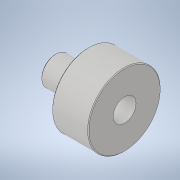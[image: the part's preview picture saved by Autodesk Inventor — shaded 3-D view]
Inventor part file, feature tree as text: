
AUTODESK INVENTOR PART (.ipt)
format: ipt  version: 2021 (Build 250183000, 183)  size: 119,808 bytes
history: native  units: in
note: dims shown in document units (in); Inventor stores cm internally (conversion verified against a paired STEP export)
features: extrude x2, sketch x2, chamfer x1
ambient origin geometry x8: Origin, YZ Plane, XZ Plane, XY Plane, X Axis, Y Axis, Z Axis, Center Point
bodies: Solid1 (feature_tree)
feature tree (5):
  extrude  "Extrusion1"  Depth=0.315in
  extrude  "Extrusion2"  Depth=0.5in
  chamfer  "Chamfer1"  Distance=0.5in
  sketch  "Sketch1"  dims[d0=0.394in d1=0.315in]
  sketch  "Sketch2"  dims[d2=0.453in d3=0.0in d4=1.0in d5=0.5in d6=0.0in d7=0.315in d9=0.01in d10=0.125in d11=45.0deg d12=0.5in d13=0.0344in d14=0.5in d15=0.0344in]
